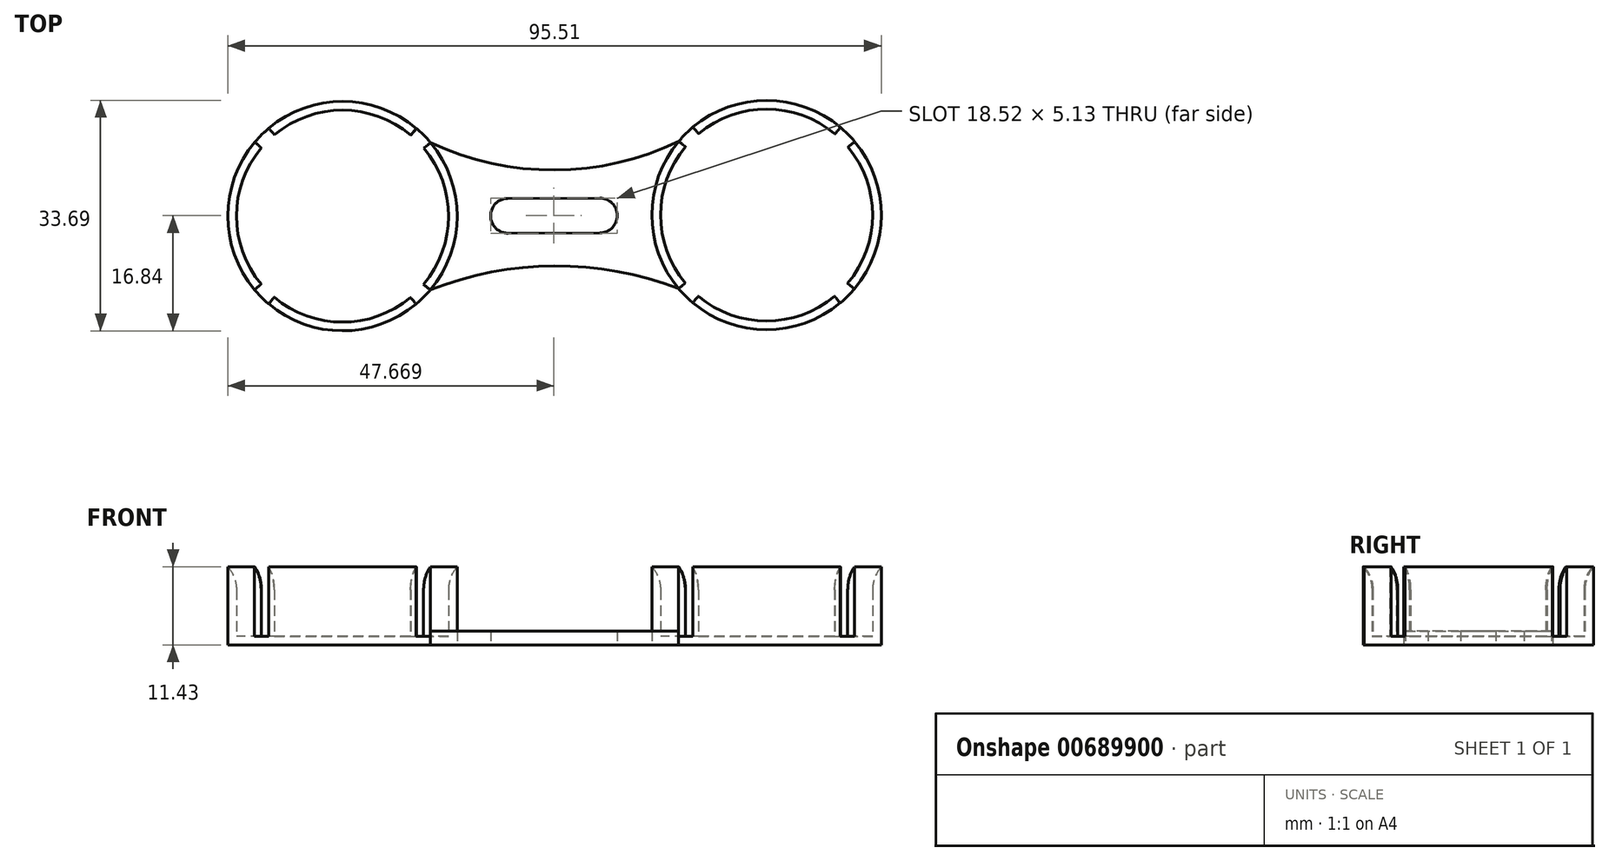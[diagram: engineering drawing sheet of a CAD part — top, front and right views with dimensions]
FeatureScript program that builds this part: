
annotation { "Feature Type Name" : "Feature", "Feature Type Description" : "" }
export const myFeature = defineFeature(function(context is Context, id is Id, definition is map)
    precondition{}
    {
        {
            var Q0;
            Q0=qCreatedBy(makeId("Top.planeOp"),FACE);
            var sketch = newSketch(context, id + "F0", { "sketchPlane" : qUnion([Q0])});
            skCircle(sketch, "E0", {"center": v(-48.01, 36.06) * mm, "radius": 15.5 * mm});
            skCircle(sketch, "E1", {"center": v(-48.01, 36.06) * mm, "radius": 16.76 * mm});
            skLineSegment(sketch, "E2", {"start": v(-38.03, 47.91) * mm, "end": v(-37.22, 48.88) * mm});
            skLineSegment(sketch, "E3", {"start": v(-36.13, 46) * mm, "end": v(-35.15, 46.81) * mm});
            skLineSegment(sketch, "E4", {"start": v(-36.16, 26.08) * mm, "end": v(-35.19, 25.26) * mm});
            skLineSegment(sketch, "E5", {"start": v(-38.07, 24.17) * mm, "end": v(-37.26, 23.2) * mm});
            skLineSegment(sketch, "E6", {"start": v(-58, 24.2) * mm, "end": v(-58.8, 23.23) * mm});
            skLineSegment(sketch, "E7", {"start": v(-59.9, 26.12) * mm, "end": v(-60.87, 25.3) * mm});
            skLineSegment(sketch, "E8", {"start": v(-59.87, 46.04) * mm, "end": v(-60.84, 46.85) * mm});
            skLineSegment(sketch, "E9", {"start": v(-57.95, 47.94) * mm, "end": v(-58.77, 48.92) * mm});
            skLineSegment(sketch, "E10", {"start": v(-17.02, 3.97) * mm, "end": v(-17.02, 72.24) * mm, "construction": true});
            skLineSegment(sketch, "E11", {"start": v(-48.01, 36.06) * mm, "end": v(-48.01, 59.97) * mm, "construction": true});
            skArc(sketch, "E12", {"start": v(2.11, 46.2) * mm, "mid": v(-1.53, 36.24) * mm, "end": v(2.08, 26.28) * mm});
            skCircle(sketch, "E13", {"center": v(13.96, 36.22) * mm, "radius": 16.76 * mm});
            skLineSegment(sketch, "E14", {"start": v(23.94, 48.07) * mm, "end": v(24.76, 49.04) * mm});
            skLineSegment(sketch, "E15", {"start": v(25.85, 46.16) * mm, "end": v(26.82, 46.97) * mm});
            skLineSegment(sketch, "E16", {"start": v(25.82, 26.24) * mm, "end": v(26.79, 25.42) * mm});
            skLineSegment(sketch, "E17", {"start": v(23.9, 24.33) * mm, "end": v(24.72, 23.36) * mm});
            skLineSegment(sketch, "E18", {"start": v(3.99, 24.36) * mm, "end": v(3.17, 23.4) * mm});
            skLineSegment(sketch, "E19", {"start": v(2.08, 26.28) * mm, "end": v(1.1, 25.46) * mm});
            skLineSegment(sketch, "E20", {"start": v(2.11, 46.2) * mm, "end": v(1.14, 47.01) * mm});
            skLineSegment(sketch, "E21", {"start": v(4.02, 48.1) * mm, "end": v(3.2, 49.07) * mm});
            skLineSegment(sketch, "E22", {"start": v(83.08, 4.86) * mm, "end": v(83.08, 73.69) * mm, "construction": true});
            skArc(sketch, "E23.trimOffspring", {"start": v(3.99, 24.36) * mm, "mid": v(13.94, 20.72) * mm, "end": v(23.9, 24.33) * mm});
            skArc(sketch, "E24.trimOffspring", {"start": v(25.82, 26.24) * mm, "mid": v(29.46, 36.2) * mm, "end": v(25.85, 46.16) * mm});
            skArc(sketch, "E25.trimOffspring", {"start": v(23.94, 48.07) * mm, "mid": v(13.99, 51.7) * mm, "end": v(4.02, 48.1) * mm});
            skLineSegment(sketch, "E26", {"start": v(13.96, 36.22) * mm, "end": v(13.96, 61.69) * mm, "construction": true});
            skLineSegment(sketch, "E27", {"start": v(-48.01, 36.02) * mm, "end": v(13.96, 36.24) * mm, "construction": true});
            skLineSegment(sketch, "E28", {"start": v(-48.01, 36.06) * mm, "end": v(-32.1, 55.02) * mm, "construction": true});
            skLineSegment(sketch, "E29", {"start": v(13.96, 36.22) * mm, "end": v(28.4, 53.41) * mm, "construction": true});
            skArc(sketch, "E30", {"start": v(-35.15, 46.81) * mm, "mid": v(-16.98, 42.8) * mm, "end": v(1.14, 47.01) * mm});
            skArc(sketch, "E31", {"start": v(1.1, 25.46) * mm, "mid": v(-17.06, 28.77) * mm, "end": v(-35.19, 25.26) * mm});
            skArc(sketch, "E32", {"start": v(-23.84, 38.65) * mm, "mid": v(-26.37, 36.1) * mm, "end": v(-23.82, 33.57) * mm});
            skArc(sketch, "E33", {"start": v(-10.38, 33.61) * mm, "mid": v(-7.85, 36.16) * mm, "end": v(-10.4, 38.7) * mm});
            skLineSegment(sketch, "E34", {"start": v(-23.84, 38.65) * mm, "end": v(-10.4, 38.7) * mm});
            skLineSegment(sketch, "E35", {"start": v(-23.82, 33.57) * mm, "end": v(-10.38, 33.61) * mm});
            skSolve(sketch);
        }
        {
            var Q0;
            {var subQ0=sQuery(id+"F0.wireOp",EDGE,"E6");Q0=makeQuery(id+"F0.imprint","IMPRINT",FACE,{"disambiguationData":[TD([[makeQuery(id+"F0.imprint","IMPRINT",EDGE,{"derivedFrom":subQ0}),-1.0]])]});}
            var Q1;
            {var subQ0=sQuery(id+"F0.wireOp",EDGE,"E4");Q1=makeQuery(id+"F0.imprint","IMPRINT",FACE,{"disambiguationData":[TD([[makeQuery(id+"F0.imprint","IMPRINT",EDGE,{"derivedFrom":subQ0}),-1.0]])]});}
            var Q2;
            {var subQ0=sQuery(id+"F0.wireOp",EDGE,"E2");Q2=makeQuery(id+"F0.imprint","IMPRINT",FACE,{"disambiguationData":[TD([[makeQuery(id+"F0.imprint","IMPRINT",EDGE,{"derivedFrom":subQ0}),-1.0]])]});}
            var Q3;
            {var subQ0=sQuery(id+"F0.wireOp",EDGE,"E8");Q3=makeQuery(id+"F0.imprint","IMPRINT",FACE,{"disambiguationData":[TD([[makeQuery(id+"F0.imprint","IMPRINT",EDGE,{"derivedFrom":subQ0}),-1.0]])]});}
            var Q4;
            {var subQ0=sQuery(id+"F0.wireOp",EDGE,"E0");var subQ4=makeQuery(id+"F0.imprint","INTERSECT",VERTEX,{"derivedFrom":[subQ0,sQuery(id+"F0.wireOp",EDGE,"E2")]});Q4=makeQuery(id+"F0.imprint","IMPRINT",FACE,{"disambiguationData":[TD([[makeQuery(id+"F0.imprint","IMPRINT",EDGE,{"disambiguationData":[TD([[subQ4,1.0]])],"derivedFrom":subQ0}),1.0]])]});}
            extrude(context, id + "F1", {"entities" : qUnion([Q0, Q1, Q2, Q3, Q4]), "depth" : 1.27 * mm, "offsetDistance" : 25.4 * mm});
        }
        {
            var Q0;
            {var subQ0=sQuery(id+"F0.wireOp",EDGE,"E7");Q0=makeQuery(id+"F0.imprint","IMPRINT",FACE,{"disambiguationData":[TD([[makeQuery(id+"F0.imprint","IMPRINT",EDGE,{"derivedFrom":subQ0}),-1.0]])]});}
            var Q1;
            {var subQ0=sQuery(id+"F0.wireOp",EDGE,"E2");Q1=makeQuery(id+"F0.imprint","IMPRINT",FACE,{"disambiguationData":[TD([[makeQuery(id+"F0.imprint","IMPRINT",EDGE,{"derivedFrom":subQ0}),1.0]])]});}
            var Q2;
            {var subQ0=sQuery(id+"F0.wireOp",EDGE,"E3");Q2=makeQuery(id+"F0.imprint","IMPRINT",FACE,{"disambiguationData":[TD([[makeQuery(id+"F0.imprint","IMPRINT",EDGE,{"derivedFrom":subQ0}),-1.0]])]});}
            var Q3;
            {var subQ0=sQuery(id+"F0.wireOp",EDGE,"E5");Q3=makeQuery(id+"F0.imprint","IMPRINT",FACE,{"disambiguationData":[TD([[makeQuery(id+"F0.imprint","IMPRINT",EDGE,{"derivedFrom":subQ0}),-1.0]])]});}
            extrude(context, id + "F2", {"entities" : qUnion([Q0, Q1, Q2, Q3]), "operationType" : NewBodyOperationType.ADD, "depth" : 11.43 * mm, "offsetDistance" : 25.4 * mm});
        }
        {
            var Q0;
            Q0=makeQuery(id+"F1.opExtrude","SWEPT_BODY",BODY,{"disambiguationData":[OSD([sQuery(id+"F0.wireOp",EDGE,"E0"),sQuery(id+"F0.wireOp",EDGE,"E1"),sQuery(id+"F0.wireOp",EDGE,"E2"),sQuery(id+"F0.wireOp",EDGE,"E3"),sQuery(id+"F0.wireOp",EDGE,"E4"),sQuery(id+"F0.wireOp",EDGE,"E5"),sQuery(id+"F0.wireOp",EDGE,"E6"),sQuery(id+"F0.wireOp",EDGE,"E7"),sQuery(id+"F0.wireOp",EDGE,"E8"),sQuery(id+"F0.wireOp",EDGE,"E9")])]});
            transform(context, id + "F3", {"entities" : qUnion([Q0]), "transformType" : TransformType.TRANSLATION_3D, "dx" : 44.96 * mm, "dy" : 0 * mm, "dz" : 0 * mm, "makeCopy" : true});
        }
        {
            var Q0;
            Q0=makeQuery(id+"F3.opPattern","COPY",BODY,{"derivedFrom":makeQuery(id+"F1.opExtrude","SWEPT_BODY",BODY,{"disambiguationData":[OSD([sQuery(id+"F0.wireOp",EDGE,"E0"),sQuery(id+"F0.wireOp",EDGE,"E1"),sQuery(id+"F0.wireOp",EDGE,"E2"),sQuery(id+"F0.wireOp",EDGE,"E3"),sQuery(id+"F0.wireOp",EDGE,"E4"),sQuery(id+"F0.wireOp",EDGE,"E5"),sQuery(id+"F0.wireOp",EDGE,"E6"),sQuery(id+"F0.wireOp",EDGE,"E7"),sQuery(id+"F0.wireOp",EDGE,"E8"),sQuery(id+"F0.wireOp",EDGE,"E9")])]}),"instanceName":"1"});
            deleteBodies(context, id + "F4", {"entities" : qUnion([Q0])});
        }
        {
            var Q0;
            Q0=makeQuery(id+"F0.imprint","IMPRINT",FACE,{"disambiguationData":[TD([[makeQuery(id+"F0.imprint","IMPRINT",EDGE,{"derivedFrom":sQuery(id+"F0.wireOp",EDGE,"E12")}),1.0]])]});
            extrude(context, id + "F5", {"entities" : qUnion([Q0]), "depth" : 1.27 * mm, "offsetDistance" : 25.4 * mm});
        }
        {
            var Q0;
            Q0=makeQuery(id+"F0.imprint","IMPRINT",FACE,{"disambiguationData":[TD([[makeQuery(id+"F0.imprint","IMPRINT",EDGE,{"derivedFrom":sQuery(id+"F0.wireOp",EDGE,"E12")}),-1.0]])]});
            var Q1;
            {var subQ0=sQuery(id+"F0.wireOp",EDGE,"E17");Q1=makeQuery(id+"F0.imprint","IMPRINT",FACE,{"disambiguationData":[TD([[makeQuery(id+"F0.imprint","IMPRINT",EDGE,{"derivedFrom":subQ0}),-1.0]])]});}
            var Q2;
            {var subQ0=sQuery(id+"F0.wireOp",EDGE,"E15");Q2=makeQuery(id+"F0.imprint","IMPRINT",FACE,{"disambiguationData":[TD([[makeQuery(id+"F0.imprint","IMPRINT",EDGE,{"derivedFrom":subQ0}),-1.0]])]});}
            var Q3;
            {var subQ0=sQuery(id+"F0.wireOp",EDGE,"E14");Q3=makeQuery(id+"F0.imprint","IMPRINT",FACE,{"disambiguationData":[TD([[makeQuery(id+"F0.imprint","IMPRINT",EDGE,{"derivedFrom":subQ0}),1.0]])]});}
            extrude(context, id + "F6", {"entities" : qUnion([Q0, Q1, Q2, Q3]), "operationType" : NewBodyOperationType.ADD, "depth" : 11.43 * mm, "offsetDistance" : 25.4 * mm});
        }
        {
            var Q0;
            {var subQ0=sQuery(id+"F0.wireOp",EDGE,"E30");Q0=makeQuery(id+"F0.imprint","IMPRINT",FACE,{"disambiguationData":[TD([[makeQuery(id+"F0.imprint","IMPRINT",EDGE,{"derivedFrom":subQ0}),-1.0]])]});}
            extrude(context, id + "F7", {"entities" : qUnion([Q0]), "depth" : 2.03 * mm, "offsetDistance" : 25.4 * mm});
        }
        {
            var Q0;
            {var subQ0=sQuery(id+"F0.wireOp",EDGE,"E0");Q0=makeQuery(id+"F2.opExtrude","CAP_EDGE",EDGE,{"disambiguationData":[OSD([subQ0]),TDD([makeQuery(id+"F0.imprint","IMPRINT",EDGE,{"disambiguationData":[TD([[makeQuery(id+"F0.imprint","INTERSECT",VERTEX,{"derivedFrom":[subQ0,sQuery(id+"F0.wireOp",EDGE,"E2")]}),-1.0]])],"derivedFrom":subQ0})])],"isStart":false});}
            var Q1;
            {var subQ0=sQuery(id+"F0.wireOp",EDGE,"E0");Q1=makeQuery(id+"F2.opExtrude","CAP_EDGE",EDGE,{"disambiguationData":[OSD([subQ0]),TDD([makeQuery(id+"F0.imprint","IMPRINT",EDGE,{"disambiguationData":[TD([[makeQuery(id+"F0.imprint","INTERSECT",VERTEX,{"derivedFrom":[subQ0,sQuery(id+"F0.wireOp",EDGE,"E7")]}),1.0]])],"derivedFrom":subQ0})])],"isStart":false});}
            var Q2;
            {var subQ0=sQuery(id+"F0.wireOp",EDGE,"E0");Q2=makeQuery(id+"F2.opExtrude","CAP_EDGE",EDGE,{"disambiguationData":[OSD([subQ0]),TDD([makeQuery(id+"F0.imprint","IMPRINT",EDGE,{"disambiguationData":[TD([[makeQuery(id+"F0.imprint","INTERSECT",VERTEX,{"derivedFrom":[subQ0,sQuery(id+"F0.wireOp",EDGE,"E3")]}),1.0]])],"derivedFrom":subQ0})])],"isStart":false});}
            var Q3;
            {var subQ0=sQuery(id+"F0.wireOp",EDGE,"E0");Q3=makeQuery(id+"F2.opExtrude","CAP_EDGE",EDGE,{"disambiguationData":[OSD([subQ0]),TDD([makeQuery(id+"F0.imprint","IMPRINT",EDGE,{"disambiguationData":[TD([[makeQuery(id+"F0.imprint","INTERSECT",VERTEX,{"derivedFrom":[subQ0,sQuery(id+"F0.wireOp",EDGE,"E5")]}),1.0]])],"derivedFrom":subQ0})])],"isStart":false});}
            var Q4;
            Q4=makeQuery(id+"F6.opExtrude","CAP_EDGE",EDGE,{"disambiguationData":[OSD([sQuery(id+"F0.wireOp",EDGE,"E12")])],"isStart":false});
            var Q5;
            Q5=makeQuery(id+"F6.opExtrude","CAP_EDGE",EDGE,{"disambiguationData":[OSD([sQuery(id+"F0.wireOp",EDGE,"E25.trimOffspring")])],"isStart":false});
            var Q6;
            Q6=makeQuery(id+"F6.opExtrude","CAP_EDGE",EDGE,{"disambiguationData":[OSD([sQuery(id+"F0.wireOp",EDGE,"E24.trimOffspring")])],"isStart":false});
            var Q7;
            Q7=makeQuery(id+"F6.opExtrude","CAP_EDGE",EDGE,{"disambiguationData":[OSD([sQuery(id+"F0.wireOp",EDGE,"E23.trimOffspring")])],"isStart":false});
            fillet(context, id + "F8", {"entities" : qUnion([Q0, Q1, Q2, Q3, Q4, Q5, Q6, Q7]), "radius" : 5.08 * mm, "tangentPropagation" : true, "allowEdgeOverflow" : false});
        }
    });
